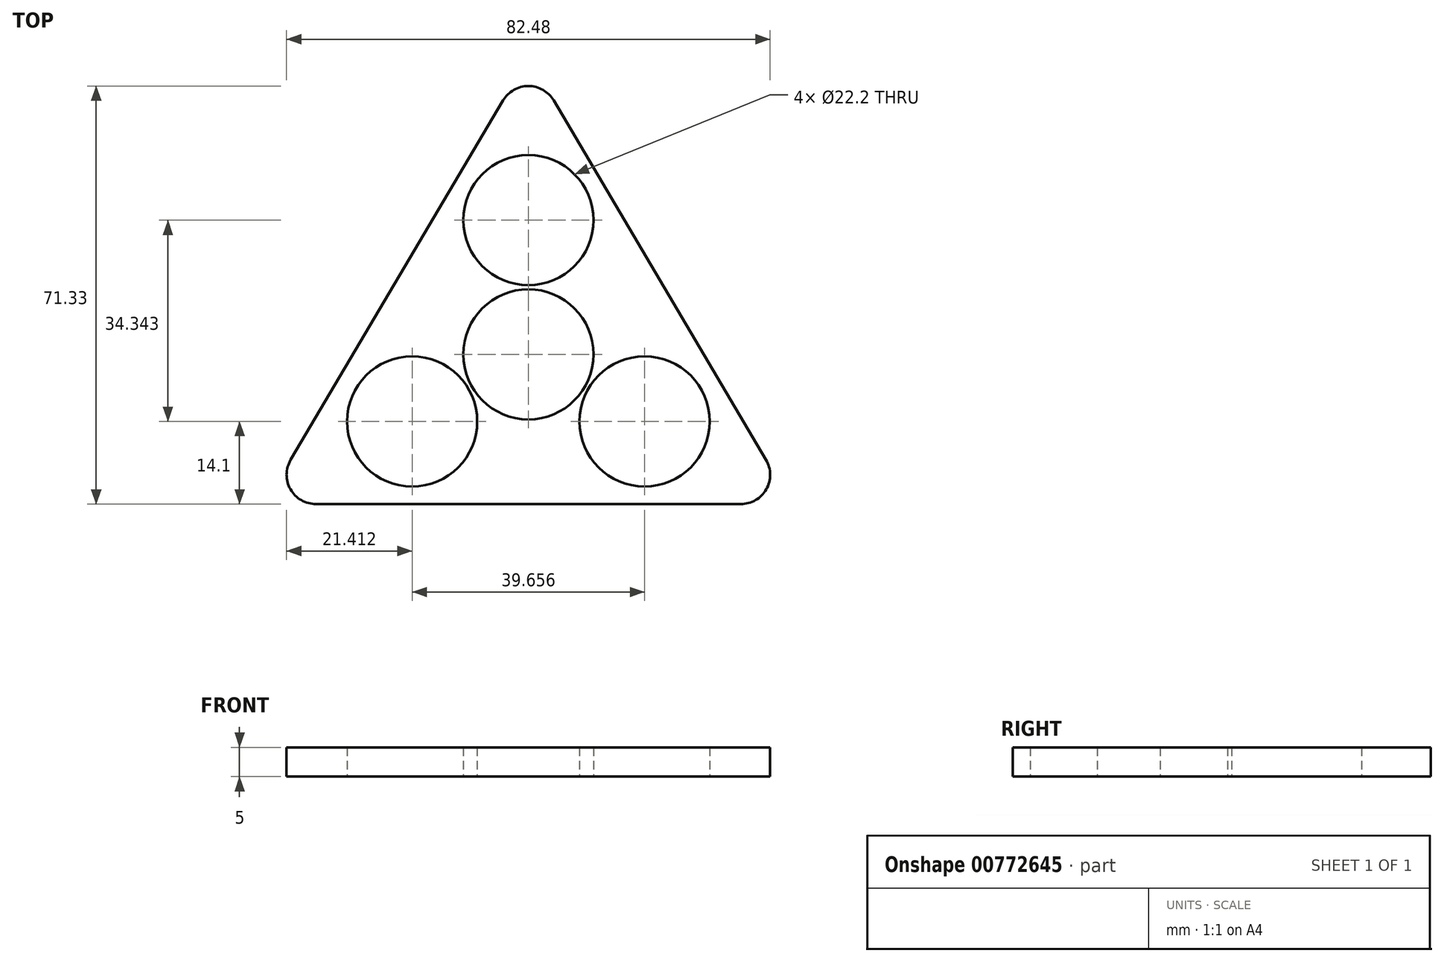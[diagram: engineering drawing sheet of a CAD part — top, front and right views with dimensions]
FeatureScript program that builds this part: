
annotation { "Feature Type Name" : "Feature", "Feature Type Description" : "" }
export const myFeature = defineFeature(function(context is Context, id is Id, definition is map)
    precondition{}
    {
        {
            var Q0;
            Q0=qCreatedBy(makeId("Top.planeOp"),FACE);
            var sketch = newSketch(context, id + "F0", { "sketchPlane" : qUnion([Q0])});
            skLineSegment(sketch, "E0", {"start": v(4.3, 68.88) * mm, "end": v(40.54, 7.54) * mm});
            skLineSegment(sketch, "E1", {"start": v(-4.3, 68.88) * mm, "end": v(-40.54, 7.54) * mm});
            skPoint(sketch, "E2.visualSharp", {"position": v(0, 76.16) * mm});
            skArc(sketch, "E2.filletArc", {"start": v(4.3, 68.88) * mm, "mid": v(0, 71.33) * mm, "end": v(-4.3, 68.88) * mm});
            skLineSegment(sketch, "E3", {"start": v(-36.24, 0) * mm, "end": v(36.24, 0) * mm});
            skPoint(sketch, "E4.visualSharp", {"position": v(-45, 0) * mm});
            skArc(sketch, "E4.filletArc", {"start": v(-40.54, 7.54) * mm, "mid": v(-40.58, 2.52) * mm, "end": v(-36.24, 0) * mm});
            skPoint(sketch, "E5.visualSharp", {"position": v(45, 0) * mm});
            skArc(sketch, "E5.filletArc", {"start": v(36.24, 0) * mm, "mid": v(40.58, 2.52) * mm, "end": v(40.54, 7.54) * mm});
            skCircle(sketch, "E6", {"center": v(0, 48.44) * mm, "radius": 11.1 * mm});
            skCircle(sketch, "E7.1.0", {"center": v(-19.83, 14.1) * mm, "radius": 11.1 * mm});
            skCircle(sketch, "E7.2.0", {"center": v(19.83, 14.1) * mm, "radius": 11.1 * mm});
            skPoint(sketch, "E7.center", {"position": v(0, 25.55) * mm});
            skCircle(sketch, "E8", {"center": v(0, 25.55) * mm, "radius": 11.1 * mm});
            skSolve(sketch);
        }
        {
            var Q0;
            Q0=makeQuery(id+"F0.imprint","IMPRINT",FACE,{"disambiguationData":[TD([[makeQuery(id+"F0.imprint","IMPRINT",EDGE,{"derivedFrom":sQuery(id+"F0.wireOp",EDGE,"E0")}),-1.0]])]});
            extrude(context, id + "F1", {"entities" : qUnion([Q0]), "depth" : 5 * mm, "offsetDistance" : 25 * mm});
        }
    });
